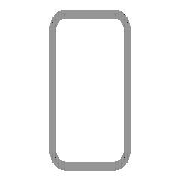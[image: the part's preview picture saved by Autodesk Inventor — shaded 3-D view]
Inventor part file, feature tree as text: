
AUTODESK INVENTOR PART (.ipt)
format: ipt  version: 2025.3 (Build 293356000, 356)  size: 134,144 bytes
history: native  units: mm (DEFAULTED — no unit token found)
features: other x4, sketch x1, plane x1
ambient origin geometry x8: Origin, YZ Plane, XZ Plane, XY Plane, X Axis, Y Axis, Z Axis, Center Point
bodies: Solid1 (feature_tree), Body (feature_tree)
feature tree (6):
  parser-record x1  (decoder bookkeeping rows leaked as tree rows — omitted from the tree; the rows remain in map.json)
  other  "Driven Length"
  other  "Start Plane"
  other  "End Plane"
  sketch  "Sketch3"  dims[d3=1210.0mm d4=0.0mm d7=6.0mm d9=40.0mm d11=80.0mm d12=3.0mm d13=20.0mm d14=1230.0mm d15=20.0mm d16=40.0mm d17=90.0deg d18=1210.0mm]
  plane  "Work Plane3"
